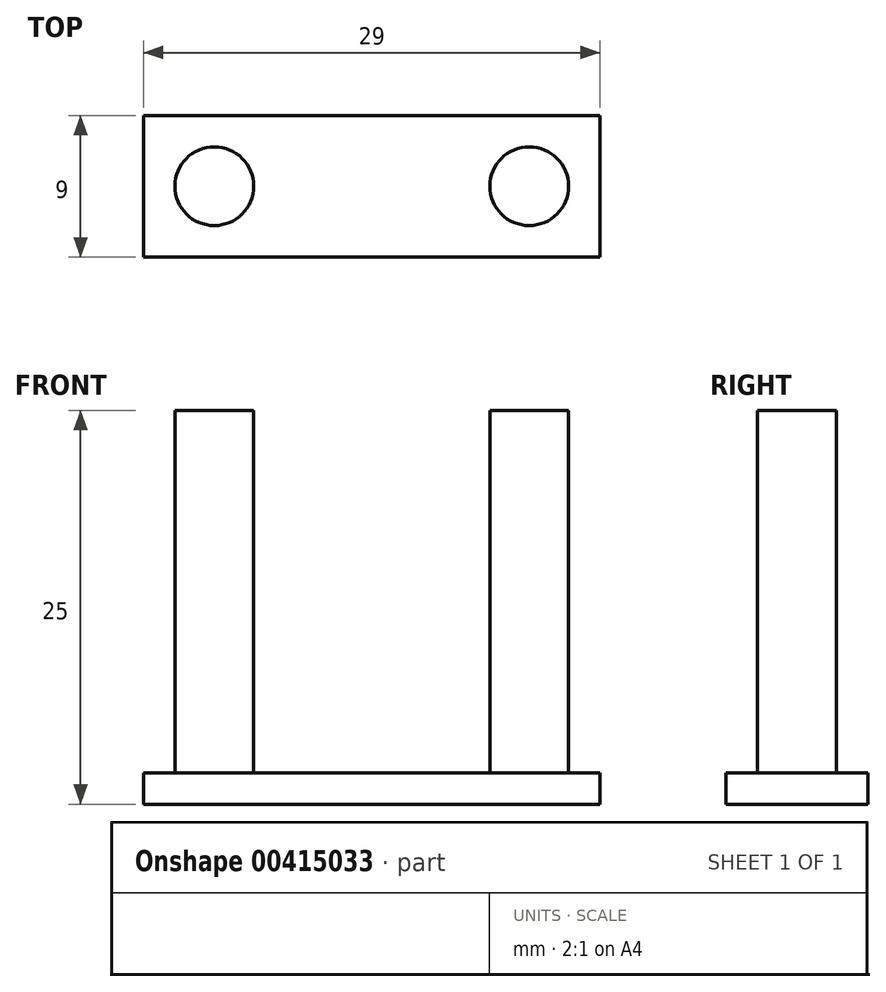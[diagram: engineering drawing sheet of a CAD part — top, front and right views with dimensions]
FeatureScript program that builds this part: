
annotation { "Feature Type Name" : "Feature", "Feature Type Description" : "" }
export const myFeature = defineFeature(function(context is Context, id is Id, definition is map)
    precondition{}
    {
        {
            var Q0;
            Q0=qCreatedBy(makeId("Top.planeOp"),FACE);
            var sketch = newSketch(context, id + "F0", { "sketchPlane" : qUnion([Q0])});
            skLineSegment(sketch, "E0.bottom", {"start": v(14.5, 4.5) * mm, "end": v(-14.5, 4.5) * mm});
            skLineSegment(sketch, "E0.top", {"start": v(14.5, -4.5) * mm, "end": v(-14.5, -4.5) * mm});
            skLineSegment(sketch, "E0.left", {"start": v(14.5, 4.5) * mm, "end": v(14.5, -4.5) * mm});
            skLineSegment(sketch, "E0.right", {"start": v(-14.5, 4.5) * mm, "end": v(-14.5, -4.5) * mm});
            skPoint(sketch, "E0.middle", {"position": v(0, 0) * mm});
            skCircle(sketch, "E1", {"center": v(-10, 0) * mm, "radius": 2.5 * mm});
            skCircle(sketch, "E2", {"center": v(10, 0) * mm, "radius": 2.5 * mm});
            skSolve(sketch);
        }
        {
            var Q0;
            Q0=makeQuery(id+"F0.imprint","IMPRINT",FACE,{"disambiguationData":[TD([[makeQuery(id+"F0.imprint","IMPRINT",EDGE,{"derivedFrom":sQuery(id+"F0.wireOp",EDGE,"E0.bottom")}),1.0]])]});
            extrude(context, id + "F1", {"entities" : qUnion([Q0]), "depth" : 2 * mm});
        }
        {
            var Q0;
            Q0=makeQuery(id+"F0.imprint","IMPRINT",FACE,{"disambiguationData":[TD([[makeQuery(id+"F0.imprint","IMPRINT",EDGE,{"derivedFrom":sQuery(id+"F0.wireOp",EDGE,"E2")}),1.0]])]});
            var Q1;
            Q1=makeQuery(id+"F0.imprint","IMPRINT",FACE,{"disambiguationData":[TD([[makeQuery(id+"F0.imprint","IMPRINT",EDGE,{"derivedFrom":sQuery(id+"F0.wireOp",EDGE,"E1")}),1.0]])]});
            extrude(context, id + "F2", {"entities" : qUnion([Q0, Q1]), "operationType" : NewBodyOperationType.ADD, "depth" : 25 * mm});
        }
    });
